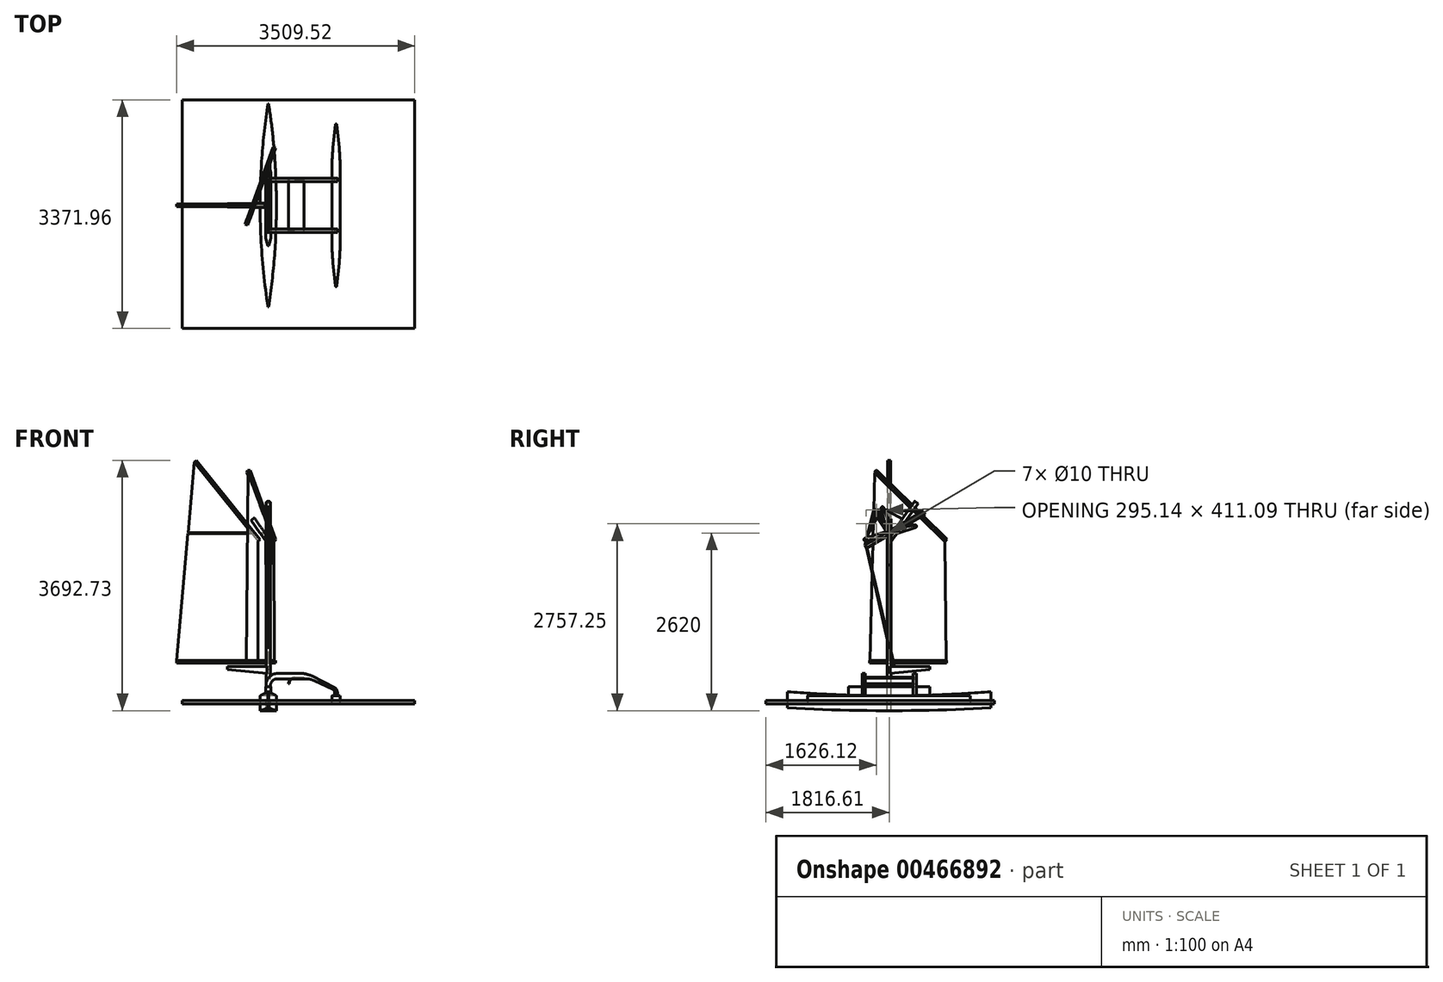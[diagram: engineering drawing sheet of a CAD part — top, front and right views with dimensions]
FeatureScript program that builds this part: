
annotation { "Feature Type Name" : "Feature", "Feature Type Description" : "" }
export const myFeature = defineFeature(function(context is Context, id is Id, definition is map)
    precondition{}
    {
        {
            var Q0;
            Q0=qCreatedBy(makeId("Top.planeOp"),FACE);
            var sketch = newSketch(context, id + "F0", { "sketchPlane" : qUnion([Q0])});
            skLineSegment(sketch, "E0", {"start": v(0, 0) * mm, "end": v(0, 1500) * mm});
            skLineSegment(sketch, "E1", {"start": v(0, 0) * mm, "end": v(120, 0) * mm});
            skLineSegment(sketch, "E2", {"start": v(120, 0) * mm, "end": v(120, -200) * mm, "construction": true});
            skLineSegment(sketch, "E3", {"start": v(0, 1500) * mm, "end": v(5, 1500) * mm});
            skArc(sketch, "E4", {"start": v(120, 0) * mm, "mid": v(91.2, 752.2) * mm, "end": v(5, 1500) * mm});
            skSolve(sketch);
        }
        {
            var Q0;
            Q0=qSketchRegion(id+"F0",true);
            extrude(context, id + "F1", {"entities" : qUnion([Q0]), "depth" : 110 * mm});
        }
        {
            var Q0;
            Q0=qCreatedBy(makeId("Right.planeOp"),FACE);
            var sketch = newSketch(context, id + "F2", { "sketchPlane" : qUnion([Q0])});
            skLineSegment(sketch, "E5.0", {"start": v(0, 0) * mm, "end": v(1500, 0) * mm});
            skLineSegment(sketch, "E6", {"start": v(1500, 0) * mm, "end": v(1500, 40) * mm});
            skLineSegment(sketch, "E7", {"start": v(0, 0) * mm, "end": v(-216.61, 0) * mm, "construction": true});
            skArc(sketch, "E8", {"start": v(0, 0) * mm, "mid": v(750.27, 10) * mm, "end": v(1500, 40) * mm});
            skSolve(sketch);
        }
        {
            var Q0;
            Q0=qSketchRegion(id+"F2",true);
            extrude(context, id + "F3", {"entities" : qUnion([Q0]), "operationType" : NewBodyOperationType.REMOVE, "depth" : 200 * mm});
        }
        {
            var Q0;
            Q0=makeQuery(id+"F1.opExtrude","SWEPT_BODY",BODY,{"disambiguationData":[OSD([sQuery(id+"F0.wireOp",EDGE,"E0"),sQuery(id+"F0.wireOp",EDGE,"E1"),sQuery(id+"F0.wireOp",EDGE,"E3"),sQuery(id+"F0.wireOp",EDGE,"E4")])]});
            var Q1;
            Q1=makeQuery(id+"F1.opExtrude","CAP_FACE",FACE,{"disambiguationData":[OSD([sQuery(id+"F0.wireOp",EDGE,"E0"),sQuery(id+"F0.wireOp",EDGE,"E1"),sQuery(id+"F0.wireOp",EDGE,"E3"),sQuery(id+"F0.wireOp",EDGE,"E4")])],"isStart":false});
            mirror(context, id + "F4", {"operationType" : NewBodyOperationType.ADD, "entities" : qUnion([Q0]), "mirrorPlane" : qUnion([Q1])});
        }
        {
            var Q0;
            Q0=makeQuery(id+"F1.opExtrude","SWEPT_BODY",BODY,{"disambiguationData":[OSD([sQuery(id+"F0.wireOp",EDGE,"E0"),sQuery(id+"F0.wireOp",EDGE,"E1"),sQuery(id+"F0.wireOp",EDGE,"E3"),sQuery(id+"F0.wireOp",EDGE,"E4")])]});
            var Q1;
            Q1=qCreatedBy(makeId("Right.planeOp"),FACE);
            mirror(context, id + "F5", {"operationType" : NewBodyOperationType.ADD, "entities" : qUnion([Q0]), "mirrorPlane" : qUnion([Q1])});
        }
        {
            var Q0;
            Q0=makeQuery(id+"F1.opExtrude","SWEPT_BODY",BODY,{"disambiguationData":[OSD([sQuery(id+"F0.wireOp",EDGE,"E0"),sQuery(id+"F0.wireOp",EDGE,"E1"),sQuery(id+"F0.wireOp",EDGE,"E3"),sQuery(id+"F0.wireOp",EDGE,"E4")])]});
            var Q1;
            Q1=qCreatedBy(makeId("Front.planeOp"),FACE);
            mirror(context, id + "F6", {"operationType" : NewBodyOperationType.ADD, "entities" : qUnion([Q0]), "mirrorPlane" : qUnion([Q1])});
        }
        {
            var Q0;
            Q0=qCreatedBy(makeId("Right.planeOp"),FACE);
            var sketch = newSketch(context, id + "F7", { "sketchPlane" : qUnion([Q0])});
            skLineSegment(sketch, "E9", {"start": v(-1500, 180) * mm, "end": v(-1500, 280) * mm});
            skLineSegment(sketch, "E10", {"start": v(1500, 180) * mm, "end": v(1500, 280) * mm});
            skLineSegment(sketch, "E11", {"start": v(0, 0) * mm, "end": v(0, 220) * mm, "construction": true});
            skArc(sketch, "E12", {"start": v(-1500, 280) * mm, "mid": v(0, 220) * mm, "end": v(1500, 280) * mm});
            skLineSegment(sketch, "E13", {"start": v(-1500, 180) * mm, "end": v(1500, 180) * mm});
            skSolve(sketch);
        }
        {
            var Q0;
            Q0=qSketchRegion(id+"F7",true);
            extrude(context, id + "F8", {"entities" : qUnion([Q0]), "operationType" : NewBodyOperationType.ADD, "depth" : 200 * mm, "hasSecondDirection" : true, "secondDirectionOppositeDirection" : true, "secondDirectionDepth" : 200 * mm});
        }
        {
            var Q0;
            Q0=makeQuery(id+"F8.opExtrude","SWEPT_FACE",FACE,{"disambiguationData":[OSD([sQuery(id+"F7.wireOp",EDGE,"E13")])]});
            var sketch = newSketch(context, id + "F9", { "sketchPlane" : qUnion([Q0])});
            skLineSegment(sketch, "E14.0", {"start": v(200, 1500) * mm, "end": v(200, -1500) * mm});
            skLineSegment(sketch, "E15.0", {"start": v(5, -1500) * mm, "end": v(-5, -1500) * mm});
            skLineSegment(sketch, "E16.0", {"start": v(-200, 1500) * mm, "end": v(-200, -1500) * mm});
            skArc(sketch, "E17.0", {"start": v(5, -1500) * mm, "mid": v(120, 0) * mm, "end": v(5, 1500) * mm});
            skArc(sketch, "E18.0", {"start": v(-5, 1500) * mm, "mid": v(-120, 0) * mm, "end": v(-5, -1500) * mm});
            skLineSegment(sketch, "E19.0", {"start": v(5, 1500) * mm, "end": v(-5, 1500) * mm});
            skLineSegment(sketch, "E20", {"start": v(-200, 1500) * mm, "end": v(-200, 1658.3) * mm});
            skLineSegment(sketch, "E21", {"start": v(-200, 1658.3) * mm, "end": v(200, 1658.3) * mm});
            skLineSegment(sketch, "E22", {"start": v(200, 1500) * mm, "end": v(200, 1658.3) * mm});
            skPoint(sketch, "E23.orphan", {"position": v(211.73, 1658.3) * mm});
            skLineSegment(sketch, "E24", {"start": v(-200, -1500) * mm, "end": v(-200, -1609.33) * mm});
            skLineSegment(sketch, "E25", {"start": v(200, -1500) * mm, "end": v(200, -1609.33) * mm});
            skLineSegment(sketch, "E26", {"start": v(-200, -1609.33) * mm, "end": v(200, -1609.33) * mm});
            skSolve(sketch);
        }
        {
            var Q0;
            Q0=qSketchRegion(id+"F9",true);
            extrude(context, id + "F10", {"entities" : qUnion([Q0]), "operationType" : NewBodyOperationType.REMOVE, "oppositeDirection" : true, "depth" : 200 * mm});
        }
        {
            var Q0;
            Q0=qCreatedBy(makeId("Top.planeOp"),FACE);
            cPlane(context, id + "F11", {"entities" : qUnion([Q0]), "cplaneType" : CPlaneType.OFFSET, "offset" : 100 * mm, "width" : 150 * mm, "height" : 150 * mm});
        }
        {
            var Q0;
            Q0=qCreatedBy(id+"F11.planeOp",FACE);
            var sketch = newSketch(context, id + "F12", { "sketchPlane" : qUnion([Q0])});
            skLineSegment(sketch, "E27.bottom", {"start": v(40, -600) * mm, "end": v(-40, -600) * mm});
            skLineSegment(sketch, "E27.top", {"start": v(40, 600) * mm, "end": v(-40, 600) * mm});
            skLineSegment(sketch, "E27.left", {"start": v(40, -600) * mm, "end": v(40, 600) * mm});
            skLineSegment(sketch, "E27.right", {"start": v(-40, -600) * mm, "end": v(-40, 600) * mm});
            skPoint(sketch, "E27.middle", {"position": v(0, 0) * mm});
            skSolve(sketch);
        }
        {
            var Q0;
            Q0=qSketchRegion(id+"F12",true);
            extrude(context, id + "F13", {"entities" : qUnion([Q0]), "operationType" : NewBodyOperationType.ADD, "depth" : 250 * mm});
        }
        {
            var Q0;
            Q0=makeQuery(id+"F13.opExtrude","SWEPT_EDGE",EDGE,{"disambiguationData":[OSD([sQuery(id+"F12.wireOp",EDGE,"E27.bottom"),sQuery(id+"F12.wireOp",EDGE,"E27.left")])]});
            var Q1;
            Q1=makeQuery(id+"F13.opExtrude","SWEPT_EDGE",EDGE,{"disambiguationData":[OSD([sQuery(id+"F12.wireOp",EDGE,"E27.bottom"),sQuery(id+"F12.wireOp",EDGE,"E27.right")])]});
            var Q2;
            Q2=makeQuery(id+"F13.opExtrude","SWEPT_EDGE",EDGE,{"disambiguationData":[OSD([sQuery(id+"F12.wireOp",EDGE,"E27.top"),sQuery(id+"F12.wireOp",EDGE,"E27.right")])]});
            var Q3;
            Q3=makeQuery(id+"F13.opExtrude","SWEPT_EDGE",EDGE,{"disambiguationData":[OSD([sQuery(id+"F12.wireOp",EDGE,"E27.top"),sQuery(id+"F12.wireOp",EDGE,"E27.left")])]});
            chamfer(context, id + "F14", {"entities" : qUnion([Q0, Q1, Q2, Q3]), "chamferType" : ChamferType.TWO_OFFSETS, "width1" : 35 * mm, "oppositeDirection" : true, "width2" : 120 * mm, "tangentPropagation" : true});
        }
        {
            var Q0;
            {var subQ0=sQuery(id+"F12.wireOp",EDGE,"E27.top");Q0=makeQuery(id+"F14.opChamfer","BLEND_EDGE",EDGE,{"blendedFrom":[makeQuery(id+"F13.opExtrude","SWEPT_EDGE",EDGE,{"disambiguationData":[OSD([subQ0,sQuery(id+"F12.wireOp",EDGE,"E27.right")])]}),makeQuery(id+"F13.opExtrude","SWEPT_FACE",FACE,{"disambiguationData":[OSD([subQ0])]})],"blendedInto":[makeQuery(id+"F13.opExtrude","SWEPT_FACE",FACE,{"disambiguationData":[OSD([subQ0])]})]});}
            var Q1;
            {var subQ0=sQuery(id+"F12.wireOp",EDGE,"E27.top");Q1=makeQuery(id+"F14.opChamfer","BLEND_EDGE",EDGE,{"blendedFrom":[makeQuery(id+"F13.opExtrude","SWEPT_EDGE",EDGE,{"disambiguationData":[OSD([subQ0,sQuery(id+"F12.wireOp",EDGE,"E27.left")])]}),makeQuery(id+"F13.opExtrude","SWEPT_FACE",FACE,{"disambiguationData":[OSD([subQ0])]})],"blendedInto":[makeQuery(id+"F13.opExtrude","SWEPT_FACE",FACE,{"disambiguationData":[OSD([subQ0])]})]});}
            var Q2;
            {var subQ0=sQuery(id+"F12.wireOp",EDGE,"E27.bottom");Q2=makeQuery(id+"F14.opChamfer","BLEND_EDGE",EDGE,{"blendedFrom":[makeQuery(id+"F13.opExtrude","SWEPT_EDGE",EDGE,{"disambiguationData":[OSD([subQ0,sQuery(id+"F12.wireOp",EDGE,"E27.right")])]}),makeQuery(id+"F13.opExtrude","SWEPT_FACE",FACE,{"disambiguationData":[OSD([subQ0])]})],"blendedInto":[makeQuery(id+"F13.opExtrude","SWEPT_FACE",FACE,{"disambiguationData":[OSD([subQ0])]})]});}
            var Q3;
            {var subQ0=sQuery(id+"F12.wireOp",EDGE,"E27.bottom");Q3=makeQuery(id+"F14.opChamfer","BLEND_EDGE",EDGE,{"blendedFrom":[makeQuery(id+"F13.opExtrude","SWEPT_EDGE",EDGE,{"disambiguationData":[OSD([subQ0,sQuery(id+"F12.wireOp",EDGE,"E27.left")])]}),makeQuery(id+"F13.opExtrude","SWEPT_FACE",FACE,{"disambiguationData":[OSD([subQ0])]})],"blendedInto":[makeQuery(id+"F13.opExtrude","SWEPT_FACE",FACE,{"disambiguationData":[OSD([subQ0])]})]});}
            fillet(context, id + "F15", {"entities" : qUnion([Q0, Q1, Q2, Q3]), "radius" : 5 * mm, "tangentPropagation" : true, "allowEdgeOverflow" : false});
        }
        {
            var Q0;
            {var subQ0=sQuery(id+"F12.wireOp",EDGE,"E27.right");Q0=makeQuery(id+"F14.opChamfer","BLEND_EDGE",EDGE,{"blendedFrom":[makeQuery(id+"F13.opExtrude","SWEPT_EDGE",EDGE,{"disambiguationData":[OSD([sQuery(id+"F12.wireOp",EDGE,"E27.bottom"),subQ0])]}),makeQuery(id+"F13.opExtrude","SWEPT_FACE",FACE,{"disambiguationData":[OSD([subQ0])]})],"blendedInto":[makeQuery(id+"F13.opExtrude","SWEPT_FACE",FACE,{"disambiguationData":[OSD([subQ0])]})]});}
            var Q1;
            {var subQ0=sQuery(id+"F12.wireOp",EDGE,"E27.left");Q1=makeQuery(id+"F14.opChamfer","BLEND_EDGE",EDGE,{"blendedFrom":[makeQuery(id+"F13.opExtrude","SWEPT_EDGE",EDGE,{"disambiguationData":[OSD([sQuery(id+"F12.wireOp",EDGE,"E27.bottom"),subQ0])]}),makeQuery(id+"F13.opExtrude","SWEPT_FACE",FACE,{"disambiguationData":[OSD([subQ0])]})],"blendedInto":[makeQuery(id+"F13.opExtrude","SWEPT_FACE",FACE,{"disambiguationData":[OSD([subQ0])]})]});}
            var Q2;
            {var subQ0=sQuery(id+"F12.wireOp",EDGE,"E27.left");Q2=makeQuery(id+"F14.opChamfer","BLEND_EDGE",EDGE,{"blendedFrom":[makeQuery(id+"F13.opExtrude","SWEPT_EDGE",EDGE,{"disambiguationData":[OSD([sQuery(id+"F12.wireOp",EDGE,"E27.top"),subQ0])]}),makeQuery(id+"F13.opExtrude","SWEPT_FACE",FACE,{"disambiguationData":[OSD([subQ0])]})],"blendedInto":[makeQuery(id+"F13.opExtrude","SWEPT_FACE",FACE,{"disambiguationData":[OSD([subQ0])]})]});}
            var Q3;
            {var subQ0=sQuery(id+"F12.wireOp",EDGE,"E27.right");Q3=makeQuery(id+"F14.opChamfer","BLEND_EDGE",EDGE,{"blendedFrom":[makeQuery(id+"F13.opExtrude","SWEPT_EDGE",EDGE,{"disambiguationData":[OSD([sQuery(id+"F12.wireOp",EDGE,"E27.top"),subQ0])]}),makeQuery(id+"F13.opExtrude","SWEPT_FACE",FACE,{"disambiguationData":[OSD([subQ0])]})],"blendedInto":[makeQuery(id+"F13.opExtrude","SWEPT_FACE",FACE,{"disambiguationData":[OSD([subQ0])]})]});}
            fillet(context, id + "F16", {"entities" : qUnion([Q0, Q1, Q2, Q3]), "radius" : 200 * mm, "tangentPropagation" : true, "allowEdgeOverflow" : false});
        }
        {
            var Q0;
            Q0=qCreatedBy(id+"F11.planeOp",FACE);
            var sketch = newSketch(context, id + "F17", { "sketchPlane" : qUnion([Q0])});
            skLineSegment(sketch, "E28.bottom", {"start": v(1060, 1200) * mm, "end": v(940, 1200) * mm});
            skLineSegment(sketch, "E28.top", {"start": v(1060, -1200) * mm, "end": v(940, -1200) * mm});
            skLineSegment(sketch, "E28.left", {"start": v(1060, 1200) * mm, "end": v(1060, -1200) * mm});
            skLineSegment(sketch, "E28.right", {"start": v(940, 1200) * mm, "end": v(940, -1200) * mm});
            skPoint(sketch, "E28.middle", {"position": v(1000, 0) * mm});
            skSolve(sketch);
        }
        {
            var Q0;
            Q0=qSketchRegion(id+"F17",true);
            extrude(context, id + "F18", {"entities" : qUnion([Q0]), "depth" : 120 * mm});
        }
        {
            var Q0;
            Q0=makeQuery(id+"F18.opExtrude","SWEPT_EDGE",EDGE,{"disambiguationData":[OSD([sQuery(id+"F17.wireOp",EDGE,"E28.top"),sQuery(id+"F17.wireOp",EDGE,"E28.right")])]});
            var Q1;
            Q1=makeQuery(id+"F18.opExtrude","SWEPT_EDGE",EDGE,{"disambiguationData":[OSD([sQuery(id+"F17.wireOp",EDGE,"E28.top"),sQuery(id+"F17.wireOp",EDGE,"E28.left")])]});
            var Q2;
            Q2=makeQuery(id+"F18.opExtrude","SWEPT_EDGE",EDGE,{"disambiguationData":[OSD([sQuery(id+"F17.wireOp",EDGE,"E28.bottom"),sQuery(id+"F17.wireOp",EDGE,"E28.right")])]});
            var Q3;
            Q3=makeQuery(id+"F18.opExtrude","SWEPT_EDGE",EDGE,{"disambiguationData":[OSD([sQuery(id+"F17.wireOp",EDGE,"E28.bottom"),sQuery(id+"F17.wireOp",EDGE,"E28.left")])]});
            chamfer(context, id + "F19", {"entities" : qUnion([Q0, Q1, Q2, Q3]), "chamferType" : ChamferType.TWO_OFFSETS, "width1" : 50 * mm, "oppositeDirection" : false, "width2" : 500 * mm, "tangentPropagation" : true});
        }
        {
            var Q0;
            {var subQ0=sQuery(id+"F17.wireOp",EDGE,"E28.top");Q0=makeQuery(id+"F19.opChamfer","BLEND_EDGE",EDGE,{"blendedFrom":[makeQuery(id+"F18.opExtrude","SWEPT_EDGE",EDGE,{"disambiguationData":[OSD([subQ0,sQuery(id+"F17.wireOp",EDGE,"E28.right")])]}),makeQuery(id+"F18.opExtrude","SWEPT_FACE",FACE,{"disambiguationData":[OSD([subQ0])]})],"blendedInto":[makeQuery(id+"F18.opExtrude","SWEPT_FACE",FACE,{"disambiguationData":[OSD([subQ0])]})]});}
            var Q1;
            {var subQ0=sQuery(id+"F17.wireOp",EDGE,"E28.top");Q1=makeQuery(id+"F19.opChamfer","BLEND_EDGE",EDGE,{"blendedFrom":[makeQuery(id+"F18.opExtrude","SWEPT_EDGE",EDGE,{"disambiguationData":[OSD([subQ0,sQuery(id+"F17.wireOp",EDGE,"E28.left")])]}),makeQuery(id+"F18.opExtrude","SWEPT_FACE",FACE,{"disambiguationData":[OSD([subQ0])]})],"blendedInto":[makeQuery(id+"F18.opExtrude","SWEPT_FACE",FACE,{"disambiguationData":[OSD([subQ0])]})]});}
            var Q2;
            {var subQ0=sQuery(id+"F17.wireOp",EDGE,"E28.bottom");Q2=makeQuery(id+"F19.opChamfer","BLEND_EDGE",EDGE,{"blendedFrom":[makeQuery(id+"F18.opExtrude","SWEPT_EDGE",EDGE,{"disambiguationData":[OSD([subQ0,sQuery(id+"F17.wireOp",EDGE,"E28.right")])]}),makeQuery(id+"F18.opExtrude","SWEPT_FACE",FACE,{"disambiguationData":[OSD([subQ0])]})],"blendedInto":[makeQuery(id+"F18.opExtrude","SWEPT_FACE",FACE,{"disambiguationData":[OSD([subQ0])]})]});}
            var Q3;
            {var subQ0=sQuery(id+"F17.wireOp",EDGE,"E28.bottom");Q3=makeQuery(id+"F19.opChamfer","BLEND_EDGE",EDGE,{"blendedFrom":[makeQuery(id+"F18.opExtrude","SWEPT_EDGE",EDGE,{"disambiguationData":[OSD([subQ0,sQuery(id+"F17.wireOp",EDGE,"E28.left")])]}),makeQuery(id+"F18.opExtrude","SWEPT_FACE",FACE,{"disambiguationData":[OSD([subQ0])]})],"blendedInto":[makeQuery(id+"F18.opExtrude","SWEPT_FACE",FACE,{"disambiguationData":[OSD([subQ0])]})]});}
            fillet(context, id + "F20", {"entities" : qUnion([Q0, Q1, Q2, Q3]), "radius" : 10 * mm, "tangentPropagation" : true, "allowEdgeOverflow" : false});
        }
        {
            var Q0;
            {var subQ0=sQuery(id+"F17.wireOp",EDGE,"E28.left");Q0=makeQuery(id+"F19.opChamfer","BLEND_EDGE",EDGE,{"blendedFrom":[makeQuery(id+"F18.opExtrude","SWEPT_EDGE",EDGE,{"disambiguationData":[OSD([sQuery(id+"F17.wireOp",EDGE,"E28.bottom"),subQ0])]}),makeQuery(id+"F18.opExtrude","SWEPT_FACE",FACE,{"disambiguationData":[OSD([subQ0])]})],"blendedInto":[makeQuery(id+"F18.opExtrude","SWEPT_FACE",FACE,{"disambiguationData":[OSD([subQ0])]})]});}
            var Q1;
            {var subQ0=sQuery(id+"F17.wireOp",EDGE,"E28.right");Q1=makeQuery(id+"F19.opChamfer","BLEND_EDGE",EDGE,{"blendedFrom":[makeQuery(id+"F18.opExtrude","SWEPT_EDGE",EDGE,{"disambiguationData":[OSD([sQuery(id+"F17.wireOp",EDGE,"E28.bottom"),subQ0])]}),makeQuery(id+"F18.opExtrude","SWEPT_FACE",FACE,{"disambiguationData":[OSD([subQ0])]})],"blendedInto":[makeQuery(id+"F18.opExtrude","SWEPT_FACE",FACE,{"disambiguationData":[OSD([subQ0])]})]});}
            var Q2;
            {var subQ0=sQuery(id+"F17.wireOp",EDGE,"E28.right");Q2=makeQuery(id+"F19.opChamfer","BLEND_EDGE",EDGE,{"blendedFrom":[makeQuery(id+"F18.opExtrude","SWEPT_EDGE",EDGE,{"disambiguationData":[OSD([sQuery(id+"F17.wireOp",EDGE,"E28.top"),subQ0])]}),makeQuery(id+"F18.opExtrude","SWEPT_FACE",FACE,{"disambiguationData":[OSD([subQ0])]})],"blendedInto":[makeQuery(id+"F18.opExtrude","SWEPT_FACE",FACE,{"disambiguationData":[OSD([subQ0])]})]});}
            var Q3;
            {var subQ0=sQuery(id+"F17.wireOp",EDGE,"E28.left");Q3=makeQuery(id+"F19.opChamfer","BLEND_EDGE",EDGE,{"blendedFrom":[makeQuery(id+"F18.opExtrude","SWEPT_EDGE",EDGE,{"disambiguationData":[OSD([sQuery(id+"F17.wireOp",EDGE,"E28.top"),subQ0])]}),makeQuery(id+"F18.opExtrude","SWEPT_FACE",FACE,{"disambiguationData":[OSD([subQ0])]})],"blendedInto":[makeQuery(id+"F18.opExtrude","SWEPT_FACE",FACE,{"disambiguationData":[OSD([subQ0])]})]});}
            fillet(context, id + "F21", {"entities" : qUnion([Q0, Q1, Q2, Q3]), "radius" : 3000 * mm, "tangentPropagation" : true, "allowEdgeOverflow" : false});
        }
        {
            var Q0;
            Q0=qCreatedBy(makeId("Front.planeOp"),FACE);
            cPlane(context, id + "F22", {"entities" : qUnion([Q0]), "cplaneType" : CPlaneType.OFFSET, "offset" : 400 * mm, "width" : 150 * mm, "height" : 150 * mm});
        }
        {
            var Q0;
            Q0=qCreatedBy(id+"F22.planeOp",FACE);
            var sketch = newSketch(context, id + "F23", { "sketchPlane" : qUnion([Q0])});
            skLineSegment(sketch, "E29", {"start": v(33.27, 350) * mm, "end": v(-33.27, 350) * mm});
            skLineSegment(sketch, "E30", {"start": v(1020, 220) * mm, "end": v(980, 220) * mm});
            skLineSegment(sketch, "E31", {"start": v(-33.27, 350) * mm, "end": v(-33.27, 380) * mm});
            skLineSegment(sketch, "E32", {"start": v(136.73, 550) * mm, "end": v(475.83, 550) * mm});
            skLineSegment(sketch, "E33", {"start": v(33.27, 350) * mm, "end": v(33.27, 370) * mm});
            skLineSegment(sketch, "E34", {"start": v(980, 220) * mm, "end": v(980, 268.3) * mm});
            skLineSegment(sketch, "E35", {"start": v(1020, 220) * mm, "end": v(1020, 270.88) * mm});
            skPoint(sketch, "E36.orphan", {"position": v(1060, 220) * mm});
            skPoint(sketch, "E37.orphan", {"position": v(940, 220) * mm});
            skLineSegment(sketch, "E38", {"start": v(647.78, 508.87) * mm, "end": v(976.2, 342.23) * mm});
            skLineSegment(sketch, "E39", {"start": v(133.27, 470) * mm, "end": v(552.25, 470) * mm});
            skLineSegment(sketch, "E40", {"start": v(680.18, 441.35) * mm, "end": v(951.32, 313.52) * mm});
            skPoint(sketch, "E41.visualSharp", {"position": v(33.27, 470) * mm});
            skArc(sketch, "E41.filletArc", {"start": v(133.27, 470) * mm, "mid": v(62.56, 440.71) * mm, "end": v(33.27, 370) * mm});
            skPoint(sketch, "E42.visualSharp", {"position": v(-33.27, 550) * mm});
            skArc(sketch, "E42.filletArc", {"start": v(136.73, 550) * mm, "mid": v(16.52, 500.2) * mm, "end": v(-33.27, 380) * mm});
            skPoint(sketch, "E43.visualSharp", {"position": v(619.42, 470) * mm});
            skArc(sketch, "E43.filletArc", {"start": v(680.18, 441.35) * mm, "mid": v(617.8, 462.75) * mm, "end": v(552.25, 470) * mm});
            skPoint(sketch, "E44.visualSharp", {"position": v(566.73, 550) * mm});
            skArc(sketch, "E44.filletArc", {"start": v(647.78, 508.87) * mm, "mid": v(564.23, 539.57) * mm, "end": v(475.83, 550) * mm});
            skPoint(sketch, "E45.visualSharp", {"position": v(980, 300) * mm});
            skArc(sketch, "E45.filletArc", {"start": v(980, 268.3) * mm, "mid": v(972.23, 295.07) * mm, "end": v(951.32, 313.52) * mm});
            skPoint(sketch, "E46.visualSharp", {"position": v(1020, 320) * mm});
            skArc(sketch, "E46.filletArc", {"start": v(1020, 270.88) * mm, "mid": v(1008.18, 312.74) * mm, "end": v(976.2, 342.23) * mm});
            skSolve(sketch);
        }
        {
            var Q0;
            Q0=qSketchRegion(id+"F23",true);
            extrude(context, id + "F24", {"entities" : qUnion([Q0]), "oppositeDirection" : true, "depth" : 50 * mm});
        }
        {
            var Q0;
            Q0=makeQuery(id+"F24.opExtrude","SWEPT_BODY",BODY,{"disambiguationData":[OSD([sQuery(id+"F23.wireOp",EDGE,"E29"),sQuery(id+"F23.wireOp",EDGE,"E30"),sQuery(id+"F23.wireOp",EDGE,"E31"),sQuery(id+"F23.wireOp",EDGE,"E32"),sQuery(id+"F23.wireOp",EDGE,"E33"),sQuery(id+"F23.wireOp",EDGE,"E34"),sQuery(id+"F23.wireOp",EDGE,"E35"),sQuery(id+"F23.wireOp",EDGE,"E38"),sQuery(id+"F23.wireOp",EDGE,"E39"),sQuery(id+"F23.wireOp",EDGE,"E40"),sQuery(id+"F23.wireOp",EDGE,"E41.filletArc"),sQuery(id+"F23.wireOp",EDGE,"E42.filletArc"),sQuery(id+"F23.wireOp",EDGE,"E43.filletArc"),sQuery(id+"F23.wireOp",EDGE,"E44.filletArc"),sQuery(id+"F23.wireOp",EDGE,"E45.filletArc"),sQuery(id+"F23.wireOp",EDGE,"E46.filletArc")])]});
            var Q1;
            Q1=qCreatedBy(makeId("Front.planeOp"),FACE);
            mirror(context, id + "F25", {"entities" : qUnion([Q0]), "mirrorPlane" : qUnion([Q1])});
        }
        {
            var Q0;
            Q0=qCreatedBy(makeId("Front.planeOp"),FACE);
            var sketch = newSketch(context, id + "F26", { "sketchPlane" : qUnion([Q0])});
            skLineSegment(sketch, "E47", {"start": v(0, 0) * mm, "end": v(0, 2500) * mm});
            skLineSegment(sketch, "E48", {"start": v(0, 2500) * mm, "end": v(-229.43, 2827.66) * mm});
            skPoint(sketch, "E49.visualSharp", {"position": v(0, 2500) * mm});
            skSolve(sketch);
        }
        {
            var Q0;
            Q0=makeQuery(id+"F13.opExtrude","CAP_FACE",FACE,{"disambiguationData":[OSD([sQuery(id+"F12.wireOp",EDGE,"E27.bottom"),sQuery(id+"F12.wireOp",EDGE,"E27.top"),sQuery(id+"F12.wireOp",EDGE,"E27.left"),sQuery(id+"F12.wireOp",EDGE,"E27.right")])],"isStart":false});
            var sketch = newSketch(context, id + "F27", { "sketchPlane" : qUnion([Q0])});
            skCircle(sketch, "E50", {"center": v(0, 0) * mm, "radius": 30 * mm});
            skSolve(sketch);
        }
        {
            var Q0;
            Q0=qSketchRegion(id+"F27",true);
            var Q1;
            Q1=qBodyType(qCreatedBy(id+"F26",EDGE),BodyType.WIRE);
            sweep(context, id + "F28", {"profiles" : qUnion([Q0]), "path" : qUnion([Q1])});
        }
        {
            var Q0;
            Q0=qCreatedBy(makeId("Front.planeOp"),FACE);
            var sketch = newSketch(context, id + "F29", { "sketchPlane" : qUnion([Q0])});
            skLineSegment(sketch, "E51", {"start": v(-118.86, 2525.11) * mm, "end": v(-1060.5, 3692.73) * mm});
            skLineSegment(sketch, "E52", {"start": v(-1060.5, 3692.73) * mm, "end": v(-1091.63, 3667.62) * mm});
            skLineSegment(sketch, "E53", {"start": v(-1091.63, 3667.62) * mm, "end": v(-150, 2500) * mm});
            skLineSegment(sketch, "E54", {"start": v(-150, 2500) * mm, "end": v(-118.86, 2525.11) * mm});
            skPoint(sketch, "E55.orphan", {"position": v(508.89, 1746.7) * mm});
            skSolve(sketch);
        }
        {
            var Q0;
            Q0=qSketchRegion(id+"F29",true);
            extrude(context, id + "F30", {"entities" : qUnion([Q0]), "depth" : 20 * mm, "hasSecondDirection" : true, "secondDirectionOppositeDirection" : true, "secondDirectionDepth" : 20 * mm});
        }
        {
            var Q0;
            Q0=qCreatedBy(makeId("Front.planeOp"),FACE);
            var sketch = newSketch(context, id + "F31", { "sketchPlane" : qUnion([Q0])});
            skLineSegment(sketch, "E56", {"start": v(0, 650) * mm, "end": v(-600, 650) * mm});
            skLineSegment(sketch, "E57", {"start": v(-600, 650) * mm, "end": v(-600, 610) * mm});
            skLineSegment(sketch, "E58", {"start": v(-600, 610) * mm, "end": v(0, 550) * mm});
            skLineSegment(sketch, "E59", {"start": v(0, 650) * mm, "end": v(0, 550) * mm});
            skSolve(sketch);
        }
        {
            var Q0;
            Q0=qSketchRegion(id+"F31",true);
            extrude(context, id + "F32", {"entities" : qUnion([Q0]), "operationType" : NewBodyOperationType.ADD, "depth" : 25 * mm, "hasSecondDirection" : true, "secondDirectionOppositeDirection" : true, "secondDirectionDepth" : 25 * mm});
        }
        {
            var Q0;
            Q0=qCreatedBy(makeId("Front.planeOp"),FACE);
            var sketch = newSketch(context, id + "F33", { "sketchPlane" : qUnion([Q0])});
            skLineSegment(sketch, "E60.bottom", {"start": v(-150, 740) * mm, "end": v(-1350, 740) * mm});
            skLineSegment(sketch, "E60.top", {"start": v(-150, 700) * mm, "end": v(-1350, 700) * mm});
            skLineSegment(sketch, "E60.left", {"start": v(-150, 740) * mm, "end": v(-150, 700) * mm});
            skLineSegment(sketch, "E60.right", {"start": v(-1350, 740) * mm, "end": v(-1350, 700) * mm});
            skSolve(sketch);
        }
        {
            var Q0;
            Q0=qSketchRegion(id+"F33",true);
            extrude(context, id + "F34", {"entities" : qUnion([Q0]), "depth" : 20 * mm, "hasSecondDirection" : true, "secondDirectionOppositeDirection" : true, "secondDirectionDepth" : 20 * mm});
        }
        {
            var Q0;
            Q0=qCreatedBy(makeId("Front.planeOp"),FACE);
            var sketch = newSketch(context, id + "F35", { "sketchPlane" : qUnion([Q0])});
            skLineSegment(sketch, "E61.0", {"start": v(-1091.63, 3667.62) * mm, "end": v(-150, 2500) * mm});
            skLineSegment(sketch, "E62.0", {"start": v(-150, 740) * mm, "end": v(-1350, 740) * mm});
            skLineSegment(sketch, "E63", {"start": v(-150, 2500) * mm, "end": v(-150, 740) * mm});
            skLineSegment(sketch, "E64", {"start": v(-1091.63, 3667.62) * mm, "end": v(-1350, 740) * mm});
            skSolve(sketch);
        }
        {
            var Q0;
            Q0=qSketchRegion(id+"F35",true);
            extrude(context, id + "F36", {"entities" : qUnion([Q0]), "depth" : .2 * mm, "hasSecondDirection" : true, "secondDirectionOppositeDirection" : true, "secondDirectionDepth" : .2 * mm});
        }
        {
            var Q0;
            Q0=qCreatedBy(makeId("Front.planeOp"),FACE);
            var sketch = newSketch(context, id + "F37", { "sketchPlane" : qUnion([Q0])});
            skLineSegment(sketch, "E65.bottom", {"start": v(310, 480) * mm, "end": v(528.88, 480) * mm});
            skLineSegment(sketch, "E65.top", {"start": v(300, 490) * mm, "end": v(528.88, 490) * mm});
            skLineSegment(sketch, "E65.left", {"start": v(300, 480) * mm, "end": v(300, 490) * mm});
            skLineSegment(sketch, "E65.right", {"start": v(528.88, 480) * mm, "end": v(528.88, 490) * mm});
            skLineSegment(sketch, "E66", {"start": v(300, 480) * mm, "end": v(300, 397.55) * mm});
            skLineSegment(sketch, "E67", {"start": v(300, 397.55) * mm, "end": v(310, 397.55) * mm});
            skLineSegment(sketch, "E68", {"start": v(310, 397.55) * mm, "end": v(310, 480) * mm});
            skSolve(sketch);
        }
        {
            var Q0;
            Q0=qSketchRegion(id+"F37",true);
            extrude(context, id + "F38", {"entities" : qUnion([Q0]), "depth" : 390 * mm, "hasSecondDirection" : true, "secondDirectionOppositeDirection" : true, "secondDirectionDepth" : 390 * mm});
        }
        {
            var Q0;
            Q0=makeQuery(id+"F38.opExtrude","SWEPT_EDGE",EDGE,{"disambiguationData":[OSD([sQuery(id+"F37.wireOp",EDGE,"E65.bottom"),sQuery(id+"F37.wireOp",EDGE,"E68")])]});
            fillet(context, id + "F39", {"entities" : qUnion([Q0]), "radius" : 80 * mm, "tangentPropagation" : true, "allowEdgeOverflow" : false});
        }
        {
            var Q0;
            Q0=makeQuery(id+"F38.opExtrude","SWEPT_EDGE",EDGE,{"disambiguationData":[OSD([sQuery(id+"F37.wireOp",EDGE,"E65.top"),sQuery(id+"F37.wireOp",EDGE,"E65.left")])]});
            fillet(context, id + "F40", {"entities" : qUnion([Q0]), "radius" : 90 * mm, "tangentPropagation" : true, "allowEdgeOverflow" : false});
        }
        {
            var Q0;
            Q0=qCreatedBy(makeId("Right.planeOp"),FACE);
            var sketch = newSketch(context, id + "F41", { "sketchPlane" : qUnion([Q0])});
            skLineSegment(sketch, "E69", {"start": v(1440.24, 469.7) * mm, "end": v(-967.66, 1898.69) * mm, "construction": true});
            skLineSegment(sketch, "E70", {"start": v(816.57, 1770.1) * mm, "end": v(408.28, 1082.12) * mm, "construction": true});
            skLineSegment(sketch, "E71", {"start": v(408.28, 1082.12) * mm, "end": v(0, 394.15) * mm, "construction": true});
            skLineSegment(sketch, "E72", {"start": v(-459.32, 1597.01) * mm, "end": v(0, 2370.98) * mm, "construction": true});
            skLineSegment(sketch, "E73", {"start": v(-459.32, 1597.01) * mm, "end": v(-918.64, 823.04) * mm, "construction": true});
            skPoint(sketch, "E74", {"position": v(-279.69, 1490.4) * mm});
            skArc(sketch, "E75", {"start": v(1440.24, 469.7) * mm, "mid": v(957.4, 1600.08) * mm, "end": v(0, 2370.98) * mm});
            skArc(sketch, "E76", {"start": v(-918.64, 823.04) * mm, "mid": v(216.7, 351.98) * mm, "end": v(1440.24, 469.7) * mm});
            skLineSegment(sketch, "E77", {"start": v(0, 0) * mm, "end": v(2000, 0) * mm, "construction": true});
            skLineSegment(sketch, "E78", {"start": v(2000, 0) * mm, "end": v(1440.24, 469.7) * mm, "construction": true});
            skArc(sketch, "E79", {"start": v(-918.64, 823.04) * mm, "mid": v(-279.69, 1490.4) * mm, "end": v(0, 2370.98) * mm});
            skSolve(sketch);
        }
        {
            var Q0;
            Q0=qCreatedBy(makeId("Right.planeOp"),FACE);
            var sketch = newSketch(context, id + "F42", { "sketchPlane" : qUnion([Q0])});
            skLineSegment(sketch, "E80", {"start": v(0, 0) * mm, "end": v(0, 2500) * mm});
            skLineSegment(sketch, "E81", {"start": v(0, 2500) * mm, "end": v(401.5, 3073.4) * mm});
            skSolve(sketch);
        }
        {
            var Q0;
            Q0=qCreatedBy(makeId("Top.planeOp"),FACE);
            var sketch = newSketch(context, id + "F43", { "sketchPlane" : qUnion([Q0])});
            skCircle(sketch, "E82", {"center": v(0, 0) * mm, "radius": 30 * mm});
            skSolve(sketch);
        }
        {
            var Q0;
            Q0 = qSketchRegion(id + "F43", true);
            var Q1;
            Q1 = qBodyType(qCreatedBy(id + "F42" ,EDGE), BodyType.WIRE);
            sweep(context, id + "F44", {"profiles" : qUnion([Q0]), "path" : qUnion([Q1])});
        }
        {
            var Q0;
            Q0=qCreatedBy(makeId("Right.planeOp"),FACE);
            var sketch = newSketch(context, id + "F45", { "sketchPlane" : qUnion([Q0])});
            skLineSegment(sketch, "E83", {"start": v(0, 650) * mm, "end": v(600, 650) * mm});
            skLineSegment(sketch, "E84", {"start": v(600, 650) * mm, "end": v(600, 610) * mm});
            skLineSegment(sketch, "E85", {"start": v(600, 610) * mm, "end": v(0, 550) * mm});
            skLineSegment(sketch, "E86", {"start": v(0, 550) * mm, "end": v(0, 650) * mm});
            skSolve(sketch);
        }
        {
            var Q0;
            Q0 = qSketchRegion(id + "F45", true);
            extrude(context, id + "F46", {"entities" : qUnion([Q0]), "operationType" : NewBodyOperationType.ADD, "depth" : 25 * mm, "hasSecondDirection" : true, "secondDirectionOppositeDirection" : true, "secondDirectionDepth" : 25 * mm});
        }
        {
            var Q0;
            Q0=makeQuery(id+"F46.opExtrude","CAP_FACE",FACE,{"disambiguationData":[OSD([sQuery(id+"F45.wireOp",EDGE,"E83"),sQuery(id+"F45.wireOp",EDGE,"E84"),sQuery(id+"F45.wireOp",EDGE,"E85"),sQuery(id+"F45.wireOp",EDGE,"E86")])],"isStart":false});
            cPlane(context, id + "F47", {"entities" : qUnion([Q0]), "cplaneType" : CPlaneType.OFFSET, "offset" : 25 * mm, "width" : 150 * mm, "height" : 150 * mm});
        }
        {
            var Q0;
            Q0=qCreatedBy(id+"F47.planeOp",FACE);
            var Q1;
            Q1=makeQuery(id+"F46.opExtrude","CAP_EDGE",EDGE,{"disambiguationData":[OSD([sQuery(id+"F45.wireOp",EDGE,"E84")])],"isStart":false});
            cPlane(context, id + "F48", {"entities" : qUnion([Q0, Q1]), "cplaneType" : CPlaneType.LINE_ANGLE, "offset" : 25 * mm, "angle" : 20 * degree, "width" : 150 * mm, "height" : 150 * mm});
        }
        {
            var Q0;
            Q0=qCreatedBy(id+"F48.planeOp",FACE);
            cPlane(context, id + "F49", {"entities" : qUnion([Q0]), "cplaneType" : CPlaneType.OFFSET, "offset" : 25 * mm, "width" : 150 * mm, "height" : 150 * mm});
        }
        {
            var Q0;
            Q0=qCreatedBy(id+"F49.planeOp",FACE);
            var sketch = newSketch(context, id + "F50", { "sketchPlane" : qUnion([Q0])});
            skLineSegment(sketch, "E87.bottom", {"start": v(377.63, 740) * mm, "end": v(-822.37, 740) * mm});
            skLineSegment(sketch, "E87.top", {"start": v(377.63, 700) * mm, "end": v(-822.37, 700) * mm});
            skLineSegment(sketch, "E87.left", {"start": v(377.63, 740) * mm, "end": v(377.63, 700) * mm});
            skLineSegment(sketch, "E87.right", {"start": v(-822.37, 740) * mm, "end": v(-822.37, 700) * mm});
            skSolve(sketch);
        }
        {
            var Q0;
            Q0 = qSketchRegion(id + "F50", true);
            extrude(context, id + "F51", {"entities" : qUnion([Q0]), "depth" : 20 * mm, "hasSecondDirection" : true, "secondDirectionOppositeDirection" : true, "secondDirectionDepth" : 20 * mm});
        }
        {
            var Q0;
            Q0=qCreatedBy(id+"F49.planeOp",FACE);
            var sketch = newSketch(context, id + "F52", { "sketchPlane" : qUnion([Q0])});
            skLineSegment(sketch, "E88", {"start": v(-827.14, 2529.38) * mm, "end": v(274.74, 3547.16) * mm});
            skLineSegment(sketch, "E89", {"start": v(274.74, 3547.16) * mm, "end": v(-827.14, 2529.38) * mm});
            skLineSegment(sketch, "E90.0", {"start": v(301.88, 3517.78) * mm, "end": v(-800, 2500) * mm});
            skLineSegment(sketch, "E91", {"start": v(-800, 2500) * mm, "end": v(-827.14, 2529.38) * mm});
            skLineSegment(sketch, "E92", {"start": v(301.88, 3517.78) * mm, "end": v(274.74, 3547.16) * mm});
            skSolve(sketch);
        }
        {
            var Q0;
            Q0 = qSketchRegion(id + "F52", true);
            extrude(context, id + "F53", {"entities" : qUnion([Q0]), "depth" : 20 * mm, "hasSecondDirection" : true, "secondDirectionOppositeDirection" : true, "secondDirectionDepth" : 20 * mm});
        }
        {
            var Q0;
            Q0=makeQuery(id+"F51.opExtrude","CAP_FACE",FACE,{"disambiguationData":[OSD([sQuery(id+"F50.wireOp",EDGE,"E87.bottom"),sQuery(id+"F50.wireOp",EDGE,"E87.top"),sQuery(id+"F50.wireOp",EDGE,"E87.left"),sQuery(id+"F50.wireOp",EDGE,"E87.right")])],"isStart":true});
            cPlane(context, id + "F54", {"entities" : qUnion([Q0]), "cplaneType" : CPlaneType.OFFSET, "offset" : 20 * mm, "oppositeDirection" : true, "width" : 150 * mm, "height" : 150 * mm});
        }
        {
            var Q0;
            Q0=qCreatedBy(id+"F54.planeOp",FACE);
            var sketch = newSketch(context, id + "F55", { "sketchPlane" : qUnion([Q0])});
            skLineSegment(sketch, "E93.0", {"start": v(-377.63, 740) * mm, "end": v(822.37, 740) * mm});
            skLineSegment(sketch, "E94.0", {"start": v(-301.88, 3517.78) * mm, "end": v(800, 2500) * mm});
            skLineSegment(sketch, "E95", {"start": v(800, 2500) * mm, "end": v(822.37, 740) * mm});
            skLineSegment(sketch, "E96", {"start": v(-301.88, 3517.78) * mm, "end": v(-377.63, 740) * mm});
            skSolve(sketch);
        }
        {
            var Q0;
            Q0 = qSketchRegion(id + "F55", true);
            extrude(context, id + "F56", {"entities" : qUnion([Q0]), "depth" : 1 * mm});
        }
        {
            var Q0;
            Q0=qCreatedBy(id+"F11.planeOp",FACE);
            var sketch = newSketch(context, id + "F57", { "sketchPlane" : qUnion([Q0])});
            skLineSegment(sketch, "E97.bottom", {"start": v(-1270, -1816.61) * mm, "end": v(2159.52, -1816.61) * mm});
            skLineSegment(sketch, "E97.top", {"start": v(-1270, 1555.35) * mm, "end": v(2159.52, 1555.35) * mm});
            skLineSegment(sketch, "E97.left", {"start": v(-1270, -1816.61) * mm, "end": v(-1270, 1555.35) * mm});
            skLineSegment(sketch, "E97.right", {"start": v(2159.52, -1816.61) * mm, "end": v(2159.52, 1555.35) * mm});
            skSolve(sketch);
        }
        {
            var Q0;
            Q0 = qSketchRegion(id + "F57", true);
            extrude(context, id + "F58", {"entities" : qUnion([Q0]), "depth" : 50 * mm});
        }
        {
            var Q0;
            Q0 = qSketchRegion(id + "F27", true);
            extrude(context, id + "F59", {"entities" : qUnion([Q0]), "depth" : 1800 * mm});
        }
        {
            var Q0;
            Q0=makeQuery(id+"F59.opExtrude","CAP_FACE",FACE,{"disambiguationData":[OSD([sQuery(id+"F27.wireOp",EDGE,"E50")])],"isStart":false});
            var sketch = newSketch(context, id + "F60", { "sketchPlane" : qUnion([Q0])});
            skLineSegment(sketch, "E98.bottom", {"start": v(40, 30) * mm, "end": v(-40, 30) * mm});
            skLineSegment(sketch, "E98.top", {"start": v(40, -30) * mm, "end": v(-40, -30) * mm});
            skLineSegment(sketch, "E98.left", {"start": v(40, 30) * mm, "end": v(40, -30) * mm});
            skLineSegment(sketch, "E98.right", {"start": v(-40, 30) * mm, "end": v(-40, -30) * mm});
            skPoint(sketch, "E98.middle", {"position": v(0, 0) * mm});
            skSolve(sketch);
        }
        {
            var Q0;
            Q0 = qSketchRegion(id + "F60", true);
            extrude(context, id + "F61", {"entities" : qUnion([Q0]), "operationType" : NewBodyOperationType.ADD, "depth" : 500 * mm});
        }
        {
            var Q0;
            Q0=makeQuery(id+"F61.opExtrude","SWEPT_FACE",FACE,{"disambiguationData":[OSD([sQuery(id+"F60.wireOp",EDGE,"E98.top")])]});
            var sketch = newSketch(context, id + "F62", { "sketchPlane" : qUnion([Q0])});
            skLineSegment(sketch, "E99.bottom", {"start": v(-10, 2350) * mm, "end": v(10, 2350) * mm});
            skLineSegment(sketch, "E99.top", {"start": v(-10, 2655) * mm, "end": v(10, 2655) * mm});
            skLineSegment(sketch, "E99.left", {"start": v(-10, 2350) * mm, "end": v(-10, 2655) * mm});
            skLineSegment(sketch, "E99.right", {"start": v(10, 2350) * mm, "end": v(10, 2655) * mm});
            skSolve(sketch);
        }
        {
            var Q0;
            Q0 = qSketchRegion(id + "F62", true);
            extrude(context, id + "F63", {"entities" : qUnion([Q0]), "operationType" : NewBodyOperationType.REMOVE, "oppositeDirection" : true, "depth" : 100 * mm});
        }
        {
            var Q0;
            Q0=makeQuery(id+"F61.opExtrude","SWEPT_FACE",FACE,{"disambiguationData":[OSD([sQuery(id+"F60.wireOp",EDGE,"E98.left")])]});
            var sketch = newSketch(context, id + "F64", { "sketchPlane" : qUnion([Q0])});
            skCircle(sketch, "E100", {"center": v(0, 2620) * mm, "radius": 5 * mm});
            skSolve(sketch);
        }
        {
            var Q0;
            Q0 = qSketchRegion(id + "F64", true);
            extrude(context, id + "F65", {"entities" : qUnion([Q0]), "operationType" : NewBodyOperationType.REMOVE, "endBound" : BoundingType.THROUGH_ALL, "oppositeDirection" : true, "depth" : 25 * mm});
        }
        {
            var Q0;
            Q0=qCreatedBy(makeId("Right.planeOp"),FACE);
            var sketch = newSketch(context, id + "F66", { "sketchPlane" : qUnion([Q0])});
            skCircle(sketch, "E101.0", {"center": v(0, 2620) * mm, "radius": 5 * mm});
            skArc(sketch, "E102", {"start": v(8.19, 2580.85) * mm, "mid": v(10.23, 2581.33) * mm, "end": v(12.25, 2581.92) * mm});
            skLineSegment(sketch, "E103", {"start": v(384.16, 2722.54) * mm, "end": v(-353.44, 2525.66) * mm, "construction": true});
            skPoint(sketch, "E104.orphan", {"position": v(0, 3303.42) * mm});
            skLineSegment(sketch, "E105", {"start": v(0, 2620) * mm, "end": v(-99, 2990.88) * mm, "construction": true});
            skArc(sketch, "E106", {"start": v(-79.97, 2997.04) * mm, "mid": v(-104.33, 3010.16) * mm, "end": v(-118.48, 2986.38) * mm});
            skArc(sketch, "E107", {"start": v(-359.63, 2544.68) * mm, "mid": v(-372.89, 2521) * mm, "end": v(-350.33, 2505.9) * mm});
            skLineSegment(sketch, "E108", {"start": v(-359.63, 2544.68) * mm, "end": v(-340.83, 2550.8) * mm});
            skLineSegment(sketch, "E109", {"start": v(-348.37, 2506.29) * mm, "end": v(8.19, 2580.85) * mm});
            skLineSegment(sketch, "E110", {"start": v(-118.55, 2986.67) * mm, "end": v(-113.88, 2965.75) * mm});
            skLineSegment(sketch, "E111", {"start": v(-79.97, 2997.04) * mm, "end": v(-73.82, 2978.04) * mm});
            skLineSegment(sketch, "E112", {"start": v(26.94, 2666.66) * mm, "end": v(356.08, 2737) * mm});
            skLineSegment(sketch, "E113", {"start": v(12.25, 2581.92) * mm, "end": v(390.28, 2703.5) * mm});
            skLineSegment(sketch, "E114", {"start": v(-99, 2990.88) * mm, "end": v(384.16, 2722.54) * mm, "construction": true});
            skLineSegment(sketch, "E115", {"start": v(-353.44, 2525.66) * mm, "end": v(-99, 2990.88) * mm, "construction": true});
            skLineSegment(sketch, "E116.0", {"start": v(-99.48, 2990) * mm, "end": v(-99.48, 2990) * mm});
            skLineSegment(sketch, "E117.0", {"start": v(-73.82, 2978.04) * mm, "end": v(359.05, 2737.63) * mm});
            skLineSegment(sketch, "E118.trimOffspring", {"start": v(-72.92, 2975.25) * mm, "end": v(26.94, 2666.66) * mm});
            skLineSegment(sketch, "E119.trimOffspring", {"start": v(-72.92, 2975.25) * mm, "end": v(356.08, 2737) * mm});
            skLineSegment(sketch, "E120.trimOffspring", {"start": v(-113.22, 2962.8) * mm, "end": v(-42.91, 2647.8) * mm});
            skLineSegment(sketch, "E121.trimOffspring", {"start": v(-98.62, 2989.48) * mm, "end": v(-98.6, 2989.52) * mm});
            skLineSegment(sketch, "E122.trimOffspring", {"start": v(-98.12, 2990.4) * mm, "end": v(-98.12, 2990.4) * mm});
            skLineSegment(sketch, "E123.trimOffspring", {"start": v(-98.64, 2989.54) * mm, "end": v(-98.6, 2989.52) * mm});
            skLineSegment(sketch, "E124.trimOffspring", {"start": v(-338.06, 2551.7) * mm, "end": v(-42.91, 2647.8) * mm});
            skLineSegment(sketch, "E125.trimOffspring", {"start": v(-338.06, 2551.7) * mm, "end": v(-113.22, 2962.8) * mm});
            skLineSegment(sketch, "E126.trimOffspring", {"start": v(-340.83, 2550.8) * mm, "end": v(-113.88, 2965.75) * mm});
            skArc(sketch, "E127.trimOffspring", {"start": v(390.28, 2703.5) * mm, "mid": v(403.48, 2727.7) * mm, "end": v(379.98, 2742.1) * mm});
            skLineSegment(sketch, "E128.trimOffspring", {"start": v(359.05, 2737.63) * mm, "end": v(379.98, 2742.1) * mm});
            skLineSegment(sketch, "E129", {"start": v(-349.35, 2506.08) * mm, "end": v(0, 1000) * mm, "construction": true});
            skLineSegment(sketch, "E130.0", {"start": v(-350.33, 2505.9) * mm, "end": v(87.55, 618.14) * mm});
            skLineSegment(sketch, "E131.0", {"start": v(-348.37, 2506.29) * mm, "end": v(89.52, 618.5) * mm});
            skLineSegment(sketch, "E132", {"start": v(89.52, 618.5) * mm, "end": v(87.55, 618.14) * mm});
            skSolve(sketch);
        }
        {
            var Q0;
            Q0 = qSketchRegion(id + "F66", true);
            extrude(context, id + "F67", {"entities" : qUnion([Q0]), "depth" : 1 * mm, "hasSecondDirection" : true, "secondDirectionOppositeDirection" : true, "secondDirectionDepth" : 1 * mm});
        }
        {
            var Q0;
            Q0=makeQuery(id+"F61.opExtrude","SWEPT_EDGE",EDGE,{"disambiguationData":[OSD([sQuery(id+"F60.wireOp",EDGE,"E98.bottom"),sQuery(id+"F60.wireOp",EDGE,"E98.left")])]});
            var Q1;
            Q1=makeQuery(id+"F61.opExtrude","SWEPT_EDGE",EDGE,{"disambiguationData":[OSD([sQuery(id+"F60.wireOp",EDGE,"E98.top"),sQuery(id+"F60.wireOp",EDGE,"E98.left")])]});
            var Q2;
            Q2=makeQuery(id+"F61.opExtrude","SWEPT_EDGE",EDGE,{"disambiguationData":[OSD([sQuery(id+"F60.wireOp",EDGE,"E98.top"),sQuery(id+"F60.wireOp",EDGE,"E98.right")])]});
            var Q3;
            Q3=makeQuery(id+"F61.opExtrude","SWEPT_EDGE",EDGE,{"disambiguationData":[OSD([sQuery(id+"F60.wireOp",EDGE,"E98.bottom"),sQuery(id+"F60.wireOp",EDGE,"E98.right")])]});
            var Q4;
            Q4=makeQuery(id+"F61.opExtrude","CAP_EDGE",EDGE,{"disambiguationData":[OSD([sQuery(id+"F60.wireOp",EDGE,"E98.right")])],"isStart":true});
            var Q5;
            Q5=makeQuery(id+"F61.opExtrude","CAP_EDGE",EDGE,{"disambiguationData":[OSD([sQuery(id+"F60.wireOp",EDGE,"E98.left")])],"isStart":true});
            fillet(context, id + "F68", {"entities" : qUnion([Q0, Q1, Q2, Q3, Q4, Q5]), "radius" : 20 * mm, "tangentPropagation" : true, "allowEdgeOverflow" : false});
        }
        {
            var Q0;
            Q0=qCreatedBy(makeId("Right.planeOp"),FACE);
            var sketch = newSketch(context, id + "F69", { "sketchPlane" : qUnion([Q0])});
            skLineSegment(sketch, "E133", {"start": v(600, 650) * mm, "end": v(0, 650) * mm});
            skLineSegment(sketch, "E134", {"start": v(0, 650) * mm, "end": v(0, 550) * mm});
            skLineSegment(sketch, "E135", {"start": v(0, 550) * mm, "end": v(600, 610) * mm});
            skLineSegment(sketch, "E136", {"start": v(600, 610) * mm, "end": v(600, 650) * mm});
            skSolve(sketch);
        }
        {
            var Q0;
            Q0 = qSketchRegion(id + "F69", true);
            extrude(context, id + "F70", {"entities" : qUnion([Q0]), "operationType" : NewBodyOperationType.ADD, "depth" : 25 * mm, "hasSecondDirection" : true, "secondDirectionOppositeDirection" : true, "secondDirectionDepth" : 25 * mm});
        }
        {
            var Q0;
            Q0=qCreatedBy(makeId("Right.planeOp"),FACE);
            var sketch = newSketch(context, id + "F71", { "sketchPlane" : qUnion([Q0])});
            skLineSegment(sketch, "E137", {"start": v(-333.23, 2398.74) * mm, "end": v(531.66, 2898.09) * mm});
            skLineSegment(sketch, "E138", {"start": v(531.66, 2898.09) * mm, "end": v(506.66, 2941.4) * mm});
            skLineSegment(sketch, "E139", {"start": v(506.66, 2941.4) * mm, "end": v(3.89, 2651.11) * mm});
            skLineSegment(sketch, "E140", {"start": v(-333.23, 2398.74) * mm, "end": v(-358.23, 2442.04) * mm});
            skCircle(sketch, "E141.0", {"center": v(0, 2620) * mm, "radius": 5 * mm});
            skLineSegment(sketch, "E142", {"start": v(0, 2620) * mm, "end": v(0, 2403.95) * mm, "construction": true});
            skLineSegment(sketch, "E143", {"start": v(0, 2620) * mm, "end": v(-237.84, 2993.12) * mm, "construction": true});
            skLineSegment(sketch, "E144.0", {"start": v(3.89, 2651.11) * mm, "end": v(-197.87, 2967.63) * mm});
            skLineSegment(sketch, "E145.0", {"start": v(-30.79, 2631.1) * mm, "end": v(-231.6, 2946.13) * mm});
            skLineSegment(sketch, "E146", {"start": v(-231.6, 2946.13) * mm, "end": v(-197.87, 2967.63) * mm});
            skLineSegment(sketch, "E147.trimOffspring", {"start": v(-30.79, 2631.1) * mm, "end": v(-358.23, 2442.04) * mm});
            skSolve(sketch);
        }
        {
            var Q0;
            Q0 = qSketchRegion(id + "F71", true);
            extrude(context, id + "F72", {"entities" : qUnion([Q0]), "depth" : 10 * mm, "hasSecondDirection" : true, "secondDirectionOppositeDirection" : true, "secondDirectionDepth" : 10 * mm});
        }
        {
            var Q0;
            Q0=qCreatedBy(makeId("Right.planeOp"),FACE);
            var sketch = newSketch(context, id + "F73", { "sketchPlane" : qUnion([Q0])});
            skLineSegment(sketch, "E148.0", {"start": v(-196.57, 2965.58) * mm, "end": v(-197.87, 2967.63) * mm});
            skLineSegment(sketch, "E149.0", {"start": v(506.66, 2941.4) * mm, "end": v(503.4, 2939.51) * mm});
            skLineSegment(sketch, "E150.0", {"start": v(-230.12, 2943.8) * mm, "end": v(-231.6, 2946.13) * mm});
            skLineSegment(sketch, "E151.0", {"start": v(-355.82, 2443.43) * mm, "end": v(-358.23, 2442.04) * mm});
            skLineSegment(sketch, "E152.0", {"start": v(-333.23, 2398.74) * mm, "end": v(-331.42, 2399.79) * mm});
            skLineSegment(sketch, "E153", {"start": v(-358.23, 2442.04) * mm, "end": v(-231.6, 2946.13) * mm});
            skLineSegment(sketch, "E154", {"start": v(-197.87, 2967.63) * mm, "end": v(506.66, 2941.4) * mm});
            skLineSegment(sketch, "E155.0", {"start": v(-196.57, 2965.58) * mm, "end": v(503.4, 2939.51) * mm});
            skLineSegment(sketch, "E156.0", {"start": v(-355.82, 2443.43) * mm, "end": v(-230.12, 2943.8) * mm});
            skPoint(sketch, "E157.orphan", {"position": v(3.89, 2651.11) * mm});
            skPoint(sketch, "E158.orphan", {"position": v(-30.79, 2631.1) * mm});
            skLineSegment(sketch, "E159", {"start": v(-333.23, 2398.74) * mm, "end": v(0, 913.97) * mm});
            skLineSegment(sketch, "E160.0", {"start": v(-331.42, 2399.79) * mm, "end": v(1.95, 914.4) * mm});
            skPoint(sketch, "E161.orphan", {"position": v(531.66, 2898.09) * mm});
            skLineSegment(sketch, "E162", {"start": v(0, 913.97) * mm, "end": v(1.95, 914.4) * mm});
            skSolve(sketch);
        }
        {
            var Q0;
            Q0 = qSketchRegion(id + "F73", true);
            extrude(context, id + "F74", {"entities" : qUnion([Q0]), "depth" : 1 * mm, "hasSecondDirection" : true, "secondDirectionOppositeDirection" : true, "secondDirectionDepth" : 1 * mm});
        }
    });
